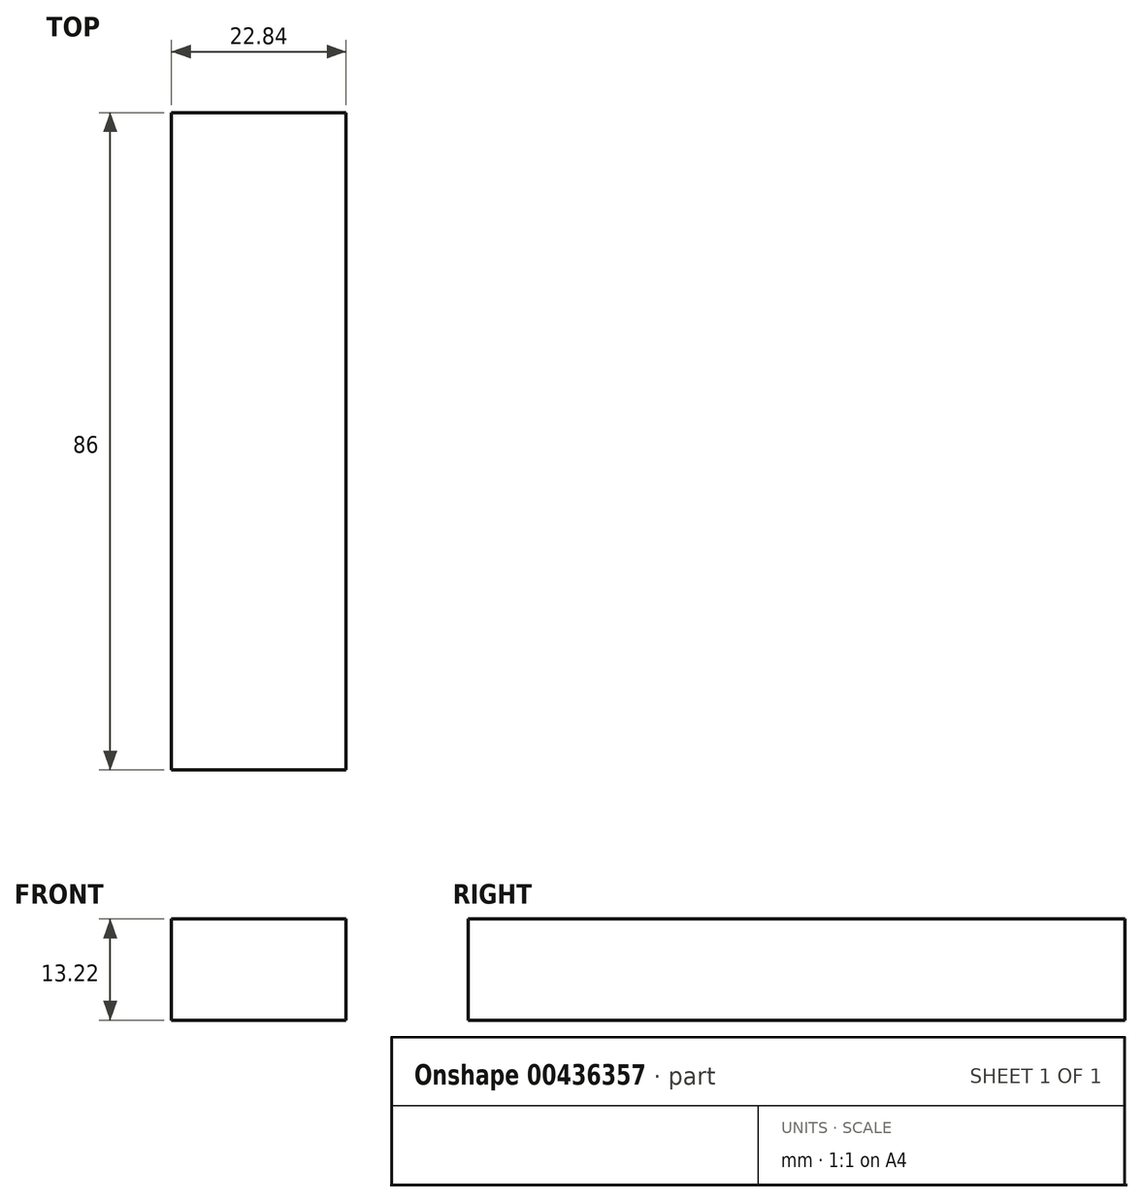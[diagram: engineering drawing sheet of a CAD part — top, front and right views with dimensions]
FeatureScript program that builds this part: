
annotation { "Feature Type Name" : "Feature", "Feature Type Description" : "" }
export const myFeature = defineFeature(function(context is Context, id is Id, definition is map)
    precondition{}
    {
        {
            var Q0;
            Q0=qCreatedBy(makeId("Front.planeOp"),FACE);
            var sketch = newSketch(context, id + "F0", { "sketchPlane" : qUnion([Q0])});
            skLineSegment(sketch, "E0.bottom", {"start": v(11.42, -6.6) * mm, "end": v(-11.42, -6.6) * mm});
            skLineSegment(sketch, "E0.top", {"start": v(11.42, 6.6) * mm, "end": v(-11.42, 6.6) * mm});
            skLineSegment(sketch, "E0.left", {"start": v(11.42, -6.6) * mm, "end": v(11.42, 6.6) * mm});
            skLineSegment(sketch, "E0.right", {"start": v(-11.42, -6.6) * mm, "end": v(-11.42, 6.6) * mm});
            skPoint(sketch, "E0.middle", {"position": v(0, 0) * mm});
            skSolve(sketch);
        }
        {
            var Q0;
            Q0 = qSketchRegion(id + "F0", true);
            extrude(context, id + "F1", {"entities" : qUnion([Q0]), "depth" : 86 * mm});
        }
    });
